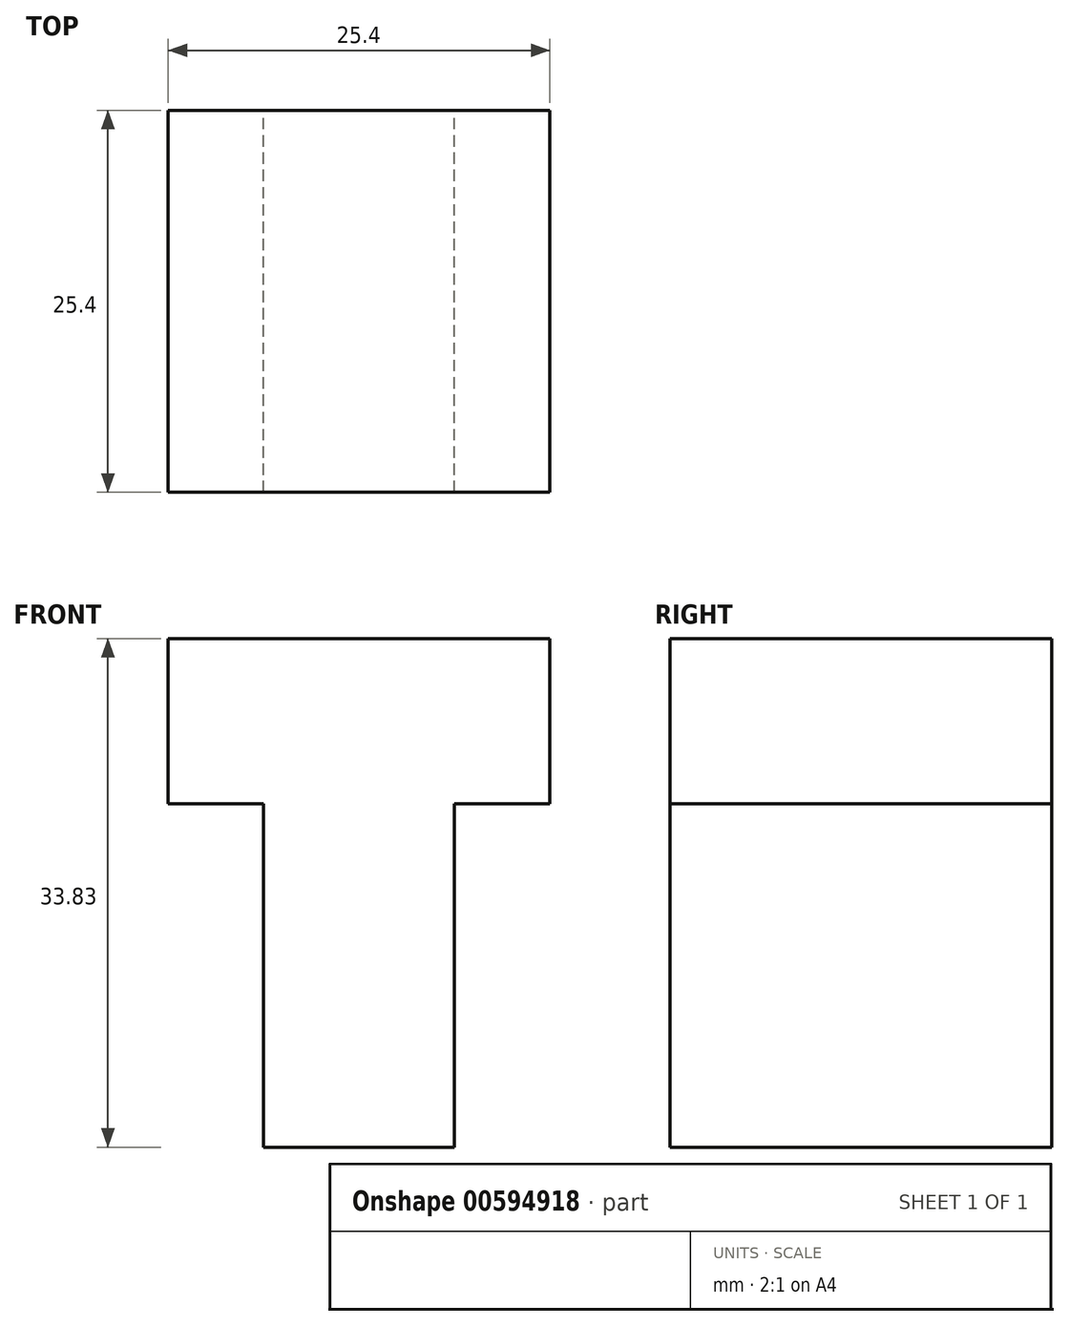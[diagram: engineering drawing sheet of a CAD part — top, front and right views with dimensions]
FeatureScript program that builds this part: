
annotation { "Feature Type Name" : "Feature", "Feature Type Description" : "" }
export const myFeature = defineFeature(function(context is Context, id is Id, definition is map)
    precondition{}
    {
        {
            var Q0;
            Q0=qCreatedBy(makeId("Front.planeOp"),FACE);
            var sketch = newSketch(context, id + "F0", { "sketchPlane" : qUnion([Q0])});
            skLineSegment(sketch, "E0", {"start": v(0, 0) * mm, "end": v(0, 22.86) * mm});
            skLineSegment(sketch, "E1", {"start": v(0, 22.86) * mm, "end": v(-6.35, 22.86) * mm});
            skLineSegment(sketch, "E2", {"start": v(-6.35, 22.86) * mm, "end": v(-6.35, 33.83) * mm});
            skLineSegment(sketch, "E3", {"start": v(-6.35, 33.83) * mm, "end": v(19.05, 33.83) * mm});
            skLineSegment(sketch, "E4", {"start": v(19.05, 33.83) * mm, "end": v(19.05, 22.86) * mm});
            skLineSegment(sketch, "E5", {"start": v(19.05, 22.86) * mm, "end": v(12.7, 22.86) * mm});
            skLineSegment(sketch, "E6", {"start": v(12.7, 22.86) * mm, "end": v(12.7, 0) * mm});
            skLineSegment(sketch, "E7", {"start": v(0, 0) * mm, "end": v(12.7, 0) * mm});
            skSolve(sketch);
        }
        {
            var Q0;
            Q0 = qSketchRegion(id + "F0", true);
            extrude(context, id + "F1", {"entities" : qUnion([Q0]), "depth" : 25.4 * mm, "offsetDistance" : 25.4 * mm});
        }
        {
            var Q0;
            Q0 = qSketchRegion(id + "F0", true);
            extrude(context, id + "F2", {"entities" : qUnion([Q0]), "operationType" : NewBodyOperationType.ADD, "depth" : 25.4 * mm, "offsetDistance" : 25.4 * mm});
        }
    });
